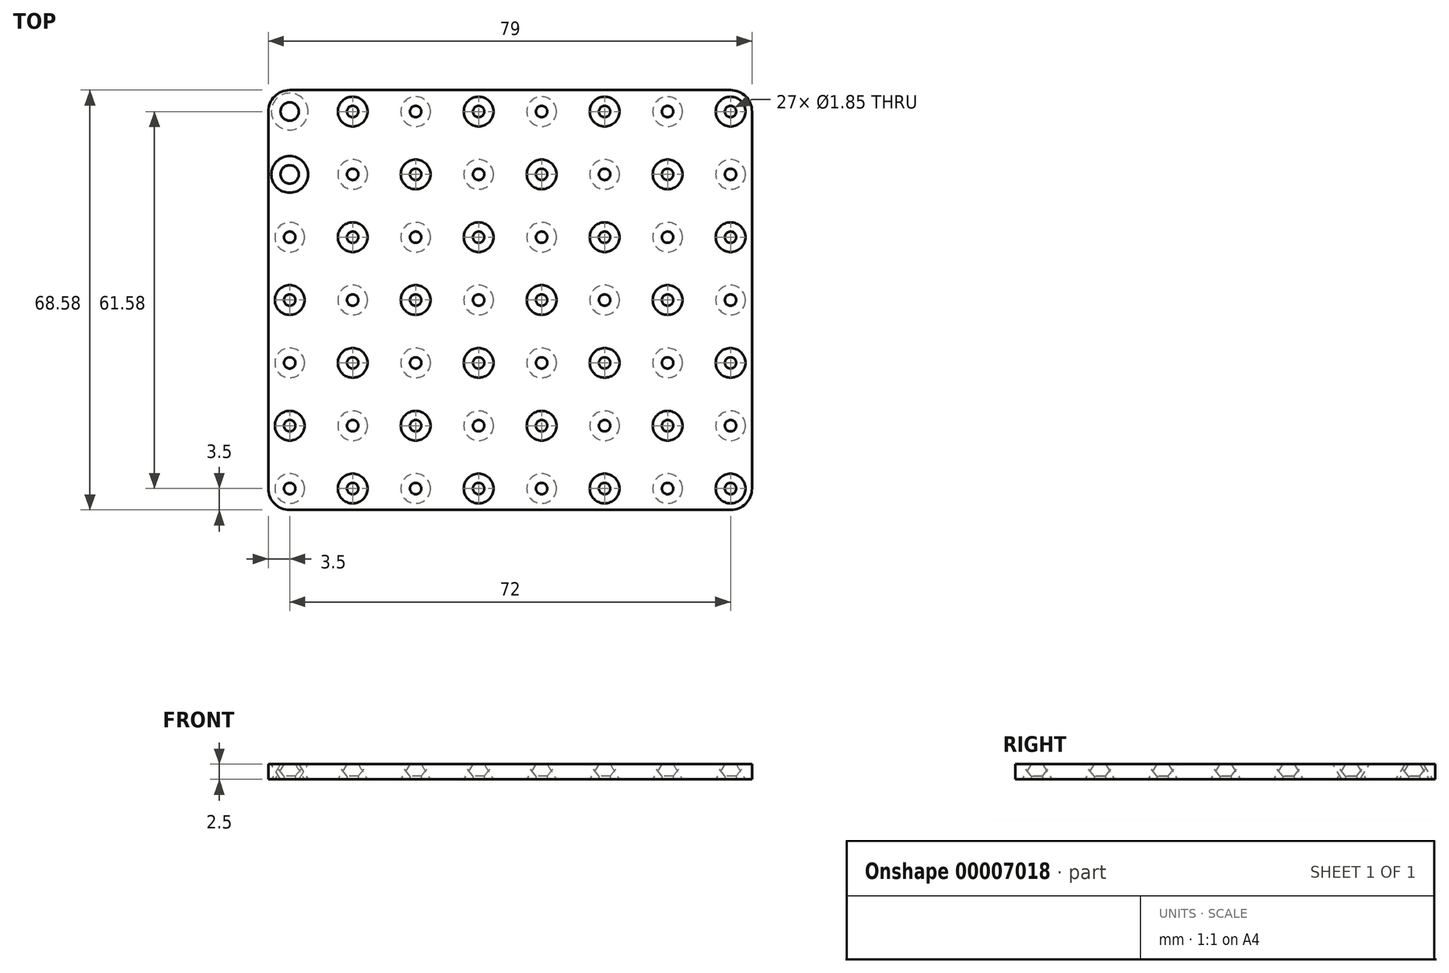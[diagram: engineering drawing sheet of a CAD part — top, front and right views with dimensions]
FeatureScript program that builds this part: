
annotation { "Feature Type Name" : "Feature", "Feature Type Description" : "" }
export const myFeature = defineFeature(function(context is Context, id is Id, definition is map)
    precondition{}
    {
        {
            var Q0;
            Q0=qCreatedBy(makeId("Top.planeOp"),FACE);
            var sketch = newSketch(context, id + "F0", { "sketchPlane" : qUnion([Q0])});
            skLineSegment(sketch, "E0.rect.bottom", {"start": v(39.5, 34.3) * mm, "end": v(-39.5, 34.3) * mm});
            skLineSegment(sketch, "E0.rect.top", {"start": v(39.5, -34.3) * mm, "end": v(-39.5, -34.3) * mm});
            skLineSegment(sketch, "E0.rect.left", {"start": v(39.5, 34.3) * mm, "end": v(39.5, -34.3) * mm});
            skLineSegment(sketch, "E0.rect.right", {"start": v(-39.5, 34.3) * mm, "end": v(-39.5, -34.3) * mm});
            skPoint(sketch, "E0.rect.middle", {"position": v(0, 0) * mm});
            skCircle(sketch, "E1", {"center": v(36, 30.8) * mm, "radius": 0.93 * mm});
            skCircle(sketch, "E2.0.1.0", {"center": v(36, 20.53) * mm, "radius": 0.93 * mm});
            skCircle(sketch, "E2.0.2.0", {"center": v(36, 10.26) * mm, "radius": 0.93 * mm});
            skCircle(sketch, "E2.0.3.0", {"center": v(36, 0) * mm, "radius": 0.93 * mm});
            skCircle(sketch, "E2.0.4.0", {"center": v(36, -10.26) * mm, "radius": 0.93 * mm});
            skCircle(sketch, "E2.0.5.0", {"center": v(36, -20.53) * mm, "radius": 0.93 * mm});
            skCircle(sketch, "E2.0.6.0", {"center": v(36, -30.8) * mm, "radius": 0.93 * mm});
            skCircle(sketch, "E2.1.0.0", {"center": v(25.71, 30.8) * mm, "radius": 0.93 * mm});
            skCircle(sketch, "E2.1.1.0", {"center": v(25.71, 20.53) * mm, "radius": 0.93 * mm});
            skCircle(sketch, "E2.1.2.0", {"center": v(25.71, 10.26) * mm, "radius": 0.93 * mm});
            skCircle(sketch, "E2.1.3.0", {"center": v(25.71, 0) * mm, "radius": 0.93 * mm});
            skCircle(sketch, "E2.1.4.0", {"center": v(25.71, -10.26) * mm, "radius": 0.93 * mm});
            skCircle(sketch, "E2.1.5.0", {"center": v(25.71, -20.53) * mm, "radius": 0.93 * mm});
            skCircle(sketch, "E2.1.6.0", {"center": v(25.71, -30.8) * mm, "radius": 0.93 * mm});
            skCircle(sketch, "E2.2.0.0", {"center": v(15.43, 30.8) * mm, "radius": 0.93 * mm});
            skCircle(sketch, "E2.2.1.0", {"center": v(15.43, 20.53) * mm, "radius": 0.93 * mm});
            skCircle(sketch, "E2.2.2.0", {"center": v(15.43, 10.26) * mm, "radius": 0.93 * mm});
            skCircle(sketch, "E2.2.3.0", {"center": v(15.43, 0) * mm, "radius": 0.93 * mm});
            skCircle(sketch, "E2.2.4.0", {"center": v(15.43, -10.26) * mm, "radius": 0.93 * mm});
            skCircle(sketch, "E2.2.5.0", {"center": v(15.43, -20.53) * mm, "radius": 0.93 * mm});
            skCircle(sketch, "E2.2.6.0", {"center": v(15.43, -30.8) * mm, "radius": 0.93 * mm});
            skCircle(sketch, "E2.3.0.0", {"center": v(5.14, 30.8) * mm, "radius": 0.93 * mm});
            skCircle(sketch, "E2.3.1.0", {"center": v(5.14, 20.53) * mm, "radius": 0.93 * mm});
            skCircle(sketch, "E2.3.2.0", {"center": v(5.14, 10.26) * mm, "radius": 0.93 * mm});
            skCircle(sketch, "E2.3.3.0", {"center": v(5.14, 0) * mm, "radius": 0.93 * mm});
            skCircle(sketch, "E2.3.4.0", {"center": v(5.14, -10.26) * mm, "radius": 0.93 * mm});
            skCircle(sketch, "E2.3.5.0", {"center": v(5.14, -20.53) * mm, "radius": 0.93 * mm});
            skCircle(sketch, "E2.3.6.0", {"center": v(5.14, -30.8) * mm, "radius": 0.93 * mm});
            skCircle(sketch, "E2.4.0.0", {"center": v(-5.14, 30.8) * mm, "radius": 0.93 * mm});
            skCircle(sketch, "E2.4.1.0", {"center": v(-5.14, 20.53) * mm, "radius": 0.93 * mm});
            skCircle(sketch, "E2.4.2.0", {"center": v(-5.14, 10.26) * mm, "radius": 0.93 * mm});
            skCircle(sketch, "E2.4.3.0", {"center": v(-5.14, 0) * mm, "radius": 0.93 * mm});
            skCircle(sketch, "E2.4.4.0", {"center": v(-5.14, -10.26) * mm, "radius": 0.93 * mm});
            skCircle(sketch, "E2.4.5.0", {"center": v(-5.14, -20.53) * mm, "radius": 0.93 * mm});
            skCircle(sketch, "E2.4.6.0", {"center": v(-5.14, -30.8) * mm, "radius": 0.93 * mm});
            skCircle(sketch, "E2.5.0.0", {"center": v(-15.43, 30.8) * mm, "radius": 0.93 * mm});
            skCircle(sketch, "E2.5.1.0", {"center": v(-15.43, 20.53) * mm, "radius": 0.93 * mm});
            skCircle(sketch, "E2.5.2.0", {"center": v(-15.43, 10.26) * mm, "radius": 0.93 * mm});
            skCircle(sketch, "E2.5.3.0", {"center": v(-15.43, 0) * mm, "radius": 0.93 * mm});
            skCircle(sketch, "E2.5.4.0", {"center": v(-15.43, -10.26) * mm, "radius": 0.93 * mm});
            skCircle(sketch, "E2.5.5.0", {"center": v(-15.43, -20.53) * mm, "radius": 0.93 * mm});
            skCircle(sketch, "E2.5.6.0", {"center": v(-15.43, -30.8) * mm, "radius": 0.93 * mm});
            skCircle(sketch, "E2.6.0.0", {"center": v(-25.71, 30.8) * mm, "radius": 0.93 * mm});
            skCircle(sketch, "E2.6.1.0", {"center": v(-25.71, 20.53) * mm, "radius": 0.93 * mm});
            skCircle(sketch, "E2.6.2.0", {"center": v(-25.71, 10.26) * mm, "radius": 0.93 * mm});
            skCircle(sketch, "E2.6.3.0", {"center": v(-25.71, 0) * mm, "radius": 0.93 * mm});
            skCircle(sketch, "E2.6.4.0", {"center": v(-25.71, -10.26) * mm, "radius": 0.93 * mm});
            skCircle(sketch, "E2.6.5.0", {"center": v(-25.71, -20.53) * mm, "radius": 0.93 * mm});
            skCircle(sketch, "E2.6.6.0", {"center": v(-25.71, -30.8) * mm, "radius": 0.93 * mm});
            skLineSegment(sketch, "E2.direction1", {"start": v(36, 30.8) * mm, "end": v(25.71, 30.8) * mm, "construction": true});
            skLineSegment(sketch, "E2.direction2", {"start": v(36, 30.8) * mm, "end": v(36, 20.53) * mm, "construction": true});
            skCircle(sketch, "E3.0.7.0", {"center": v(-36, 30.8) * mm, "radius": 0.93 * mm});
            skCircle(sketch, "E3.0.7.1", {"center": v(-36, 20.53) * mm, "radius": 0.93 * mm});
            skCircle(sketch, "E3.0.7.2", {"center": v(-36, 10.26) * mm, "radius": 0.93 * mm});
            skCircle(sketch, "E3.0.7.3", {"center": v(-36, 0) * mm, "radius": 0.93 * mm});
            skCircle(sketch, "E3.0.7.4", {"center": v(-36, -10.26) * mm, "radius": 0.93 * mm});
            skCircle(sketch, "E3.0.7.5", {"center": v(-36, -20.53) * mm, "radius": 0.93 * mm});
            skCircle(sketch, "E3.0.7.6", {"center": v(-36, -30.8) * mm, "radius": 0.93 * mm});
            skSolve(sketch);
        }
        {
            var Q0;
            Q0=makeQuery(id+"F0.imprint","IMPRINT",FACE,{"disambiguationData":[TD([[makeQuery(id+"F0.imprint","IMPRINT",EDGE,{"derivedFrom":sQuery(id+"F0.wireOp",EDGE,"E0.rect.bottom")}),1.0]])]});
            extrude(context, id + "F1", {"entities" : qUnion([Q0]), "endBound" : BoundingType.SYMMETRIC, "depth" : 2.5 * mm});
        }
        {
            var Q0;
            Q0=makeQuery(id+"F1.opExtrude","SWEPT_EDGE",EDGE,{"disambiguationData":[OSD([sQuery(id+"F0.wireOp",EDGE,"E0.rect.top"),sQuery(id+"F0.wireOp",EDGE,"E0.rect.left")])]});
            var Q1;
            Q1=makeQuery(id+"F1.opExtrude","SWEPT_EDGE",EDGE,{"disambiguationData":[OSD([sQuery(id+"F0.wireOp",EDGE,"E0.rect.top"),sQuery(id+"F0.wireOp",EDGE,"E0.rect.right")])]});
            var Q2;
            Q2=makeQuery(id+"F1.opExtrude","SWEPT_EDGE",EDGE,{"disambiguationData":[OSD([sQuery(id+"F0.wireOp",EDGE,"E0.rect.bottom"),sQuery(id+"F0.wireOp",EDGE,"E0.rect.right")])]});
            var Q3;
            Q3=makeQuery(id+"F1.opExtrude","SWEPT_EDGE",EDGE,{"disambiguationData":[OSD([sQuery(id+"F0.wireOp",EDGE,"E0.rect.bottom"),sQuery(id+"F0.wireOp",EDGE,"E0.rect.left")])]});
            fillet(context, id + "F2", {"entities" : qUnion([Q0, Q1, Q2, Q3]), "radius" : 3.5 * mm, "tangentPropagation" : true, "allowEdgeOverflow" : false});
        }
        {
            var Q0;
            {var subQ0=sQuery(id+"F0.wireOp",EDGE,"E0.rect.bottom");var subQ1=sQuery(id+"F0.wireOp",EDGE,"E0.rect.right");Q0=makeQuery(id+"F2.opFillet","BLEND_VERTEX",VERTEX,{"blendedFrom":[makeQuery(id+"F1.opExtrude","SWEPT_EDGE",EDGE,{"disambiguationData":[OSD([subQ0,subQ1])]}),makeQuery(id+"F1.opExtrude","SWEPT_FACE",FACE,{"disambiguationData":[OSD([subQ0])]}),makeQuery(id+"F1.opExtrude","CAP_FACE",FACE,{"disambiguationData":[OSD([subQ0,sQuery(id+"F0.wireOp",EDGE,"E0.rect.top"),sQuery(id+"F0.wireOp",EDGE,"E0.rect.left"),subQ1,sQuery(id+"F0.wireOp",EDGE,"E1"),sQuery(id+"F0.wireOp",EDGE,"E2.0.1.0"),sQuery(id+"F0.wireOp",EDGE,"E2.0.2.0"),sQuery(id+"F0.wireOp",EDGE,"E2.0.3.0"),sQuery(id+"F0.wireOp",EDGE,"E2.0.4.0"),sQuery(id+"F0.wireOp",EDGE,"E2.0.5.0"),sQuery(id+"F0.wireOp",EDGE,"E2.0.6.0"),sQuery(id+"F0.wireOp",EDGE,"E2.0.7.0"),sQuery(id+"F0.wireOp",EDGE,"E2.1.0.0"),sQuery(id+"F0.wireOp",EDGE,"E2.1.1.0"),sQuery(id+"F0.wireOp",EDGE,"E2.1.2.0"),sQuery(id+"F0.wireOp",EDGE,"E2.1.3.0"),sQuery(id+"F0.wireOp",EDGE,"E2.1.4.0"),sQuery(id+"F0.wireOp",EDGE,"E2.1.5.0"),sQuery(id+"F0.wireOp",EDGE,"E2.1.6.0"),sQuery(id+"F0.wireOp",EDGE,"E2.1.7.0"),sQuery(id+"F0.wireOp",EDGE,"E2.2.0.0"),sQuery(id+"F0.wireOp",EDGE,"E2.2.1.0"),sQuery(id+"F0.wireOp",EDGE,"E2.2.2.0"),sQuery(id+"F0.wireOp",EDGE,"E2.2.3.0"),sQuery(id+"F0.wireOp",EDGE,"E2.2.4.0"),sQuery(id+"F0.wireOp",EDGE,"E2.2.5.0"),sQuery(id+"F0.wireOp",EDGE,"E2.2.6.0"),sQuery(id+"F0.wireOp",EDGE,"E2.2.7.0"),sQuery(id+"F0.wireOp",EDGE,"E2.3.0.0"),sQuery(id+"F0.wireOp",EDGE,"E2.3.1.0"),sQuery(id+"F0.wireOp",EDGE,"E2.3.2.0"),sQuery(id+"F0.wireOp",EDGE,"E2.3.3.0"),sQuery(id+"F0.wireOp",EDGE,"E2.3.4.0"),sQuery(id+"F0.wireOp",EDGE,"E2.3.5.0"),sQuery(id+"F0.wireOp",EDGE,"E2.3.6.0"),sQuery(id+"F0.wireOp",EDGE,"E2.3.7.0"),sQuery(id+"F0.wireOp",EDGE,"E2.4.0.0"),sQuery(id+"F0.wireOp",EDGE,"E2.4.1.0"),sQuery(id+"F0.wireOp",EDGE,"E2.4.2.0"),sQuery(id+"F0.wireOp",EDGE,"E2.4.3.0"),sQuery(id+"F0.wireOp",EDGE,"E2.4.4.0"),sQuery(id+"F0.wireOp",EDGE,"E2.4.5.0"),sQuery(id+"F0.wireOp",EDGE,"E2.4.6.0"),sQuery(id+"F0.wireOp",EDGE,"E2.4.7.0"),sQuery(id+"F0.wireOp",EDGE,"E2.5.0.0"),sQuery(id+"F0.wireOp",EDGE,"E2.5.1.0"),sQuery(id+"F0.wireOp",EDGE,"E2.5.2.0"),sQuery(id+"F0.wireOp",EDGE,"E2.5.3.0"),sQuery(id+"F0.wireOp",EDGE,"E2.5.4.0"),sQuery(id+"F0.wireOp",EDGE,"E2.5.5.0"),sQuery(id+"F0.wireOp",EDGE,"E2.5.6.0"),sQuery(id+"F0.wireOp",EDGE,"E2.5.7.0"),sQuery(id+"F0.wireOp",EDGE,"E2.6.0.0"),sQuery(id+"F0.wireOp",EDGE,"E2.6.1.0"),sQuery(id+"F0.wireOp",EDGE,"E2.6.2.0"),sQuery(id+"F0.wireOp",EDGE,"E2.6.3.0"),sQuery(id+"F0.wireOp",EDGE,"E2.6.4.0"),sQuery(id+"F0.wireOp",EDGE,"E2.6.5.0"),sQuery(id+"F0.wireOp",EDGE,"E2.6.6.0"),sQuery(id+"F0.wireOp",EDGE,"E2.6.7.0")])],"isStart":true})],"blendedInto":[makeQuery(id+"F1.opExtrude","SWEPT_FACE",FACE,{"disambiguationData":[OSD([subQ0])]}),makeQuery(id+"F1.opExtrude","CAP_FACE",FACE,{"disambiguationData":[OSD([subQ0,sQuery(id+"F0.wireOp",EDGE,"E0.rect.top"),sQuery(id+"F0.wireOp",EDGE,"E0.rect.left"),subQ1,sQuery(id+"F0.wireOp",EDGE,"E1"),sQuery(id+"F0.wireOp",EDGE,"E2.0.1.0"),sQuery(id+"F0.wireOp",EDGE,"E2.0.2.0"),sQuery(id+"F0.wireOp",EDGE,"E2.0.3.0"),sQuery(id+"F0.wireOp",EDGE,"E2.0.4.0"),sQuery(id+"F0.wireOp",EDGE,"E2.0.5.0"),sQuery(id+"F0.wireOp",EDGE,"E2.0.6.0"),sQuery(id+"F0.wireOp",EDGE,"E2.0.7.0"),sQuery(id+"F0.wireOp",EDGE,"E2.1.0.0"),sQuery(id+"F0.wireOp",EDGE,"E2.1.1.0"),sQuery(id+"F0.wireOp",EDGE,"E2.1.2.0"),sQuery(id+"F0.wireOp",EDGE,"E2.1.3.0"),sQuery(id+"F0.wireOp",EDGE,"E2.1.4.0"),sQuery(id+"F0.wireOp",EDGE,"E2.1.5.0"),sQuery(id+"F0.wireOp",EDGE,"E2.1.6.0"),sQuery(id+"F0.wireOp",EDGE,"E2.1.7.0"),sQuery(id+"F0.wireOp",EDGE,"E2.2.0.0"),sQuery(id+"F0.wireOp",EDGE,"E2.2.1.0"),sQuery(id+"F0.wireOp",EDGE,"E2.2.2.0"),sQuery(id+"F0.wireOp",EDGE,"E2.2.3.0"),sQuery(id+"F0.wireOp",EDGE,"E2.2.4.0"),sQuery(id+"F0.wireOp",EDGE,"E2.2.5.0"),sQuery(id+"F0.wireOp",EDGE,"E2.2.6.0"),sQuery(id+"F0.wireOp",EDGE,"E2.2.7.0"),sQuery(id+"F0.wireOp",EDGE,"E2.3.0.0"),sQuery(id+"F0.wireOp",EDGE,"E2.3.1.0"),sQuery(id+"F0.wireOp",EDGE,"E2.3.2.0"),sQuery(id+"F0.wireOp",EDGE,"E2.3.3.0"),sQuery(id+"F0.wireOp",EDGE,"E2.3.4.0"),sQuery(id+"F0.wireOp",EDGE,"E2.3.5.0"),sQuery(id+"F0.wireOp",EDGE,"E2.3.6.0"),sQuery(id+"F0.wireOp",EDGE,"E2.3.7.0"),sQuery(id+"F0.wireOp",EDGE,"E2.4.0.0"),sQuery(id+"F0.wireOp",EDGE,"E2.4.1.0"),sQuery(id+"F0.wireOp",EDGE,"E2.4.2.0"),sQuery(id+"F0.wireOp",EDGE,"E2.4.3.0"),sQuery(id+"F0.wireOp",EDGE,"E2.4.4.0"),sQuery(id+"F0.wireOp",EDGE,"E2.4.5.0"),sQuery(id+"F0.wireOp",EDGE,"E2.4.6.0"),sQuery(id+"F0.wireOp",EDGE,"E2.4.7.0"),sQuery(id+"F0.wireOp",EDGE,"E2.5.0.0"),sQuery(id+"F0.wireOp",EDGE,"E2.5.1.0"),sQuery(id+"F0.wireOp",EDGE,"E2.5.2.0"),sQuery(id+"F0.wireOp",EDGE,"E2.5.3.0"),sQuery(id+"F0.wireOp",EDGE,"E2.5.4.0"),sQuery(id+"F0.wireOp",EDGE,"E2.5.5.0"),sQuery(id+"F0.wireOp",EDGE,"E2.5.6.0"),sQuery(id+"F0.wireOp",EDGE,"E2.5.7.0"),sQuery(id+"F0.wireOp",EDGE,"E2.6.0.0"),sQuery(id+"F0.wireOp",EDGE,"E2.6.1.0"),sQuery(id+"F0.wireOp",EDGE,"E2.6.2.0"),sQuery(id+"F0.wireOp",EDGE,"E2.6.3.0"),sQuery(id+"F0.wireOp",EDGE,"E2.6.4.0"),sQuery(id+"F0.wireOp",EDGE,"E2.6.5.0"),sQuery(id+"F0.wireOp",EDGE,"E2.6.6.0"),sQuery(id+"F0.wireOp",EDGE,"E2.6.7.0")])],"isStart":true})]});}
            var Q1;
            {var subQ0=sQuery(id+"F0.wireOp",EDGE,"E0.rect.bottom");var subQ1=sQuery(id+"F0.wireOp",EDGE,"E0.rect.right");Q1=makeQuery(id+"F2.opFillet","BLEND_VERTEX",VERTEX,{"blendedFrom":[makeQuery(id+"F1.opExtrude","SWEPT_EDGE",EDGE,{"disambiguationData":[OSD([subQ0,subQ1])]}),makeQuery(id+"F1.opExtrude","SWEPT_FACE",FACE,{"disambiguationData":[OSD([subQ0])]}),makeQuery(id+"F1.opExtrude","CAP_FACE",FACE,{"disambiguationData":[OSD([subQ0,sQuery(id+"F0.wireOp",EDGE,"E0.rect.top"),sQuery(id+"F0.wireOp",EDGE,"E0.rect.left"),subQ1,sQuery(id+"F0.wireOp",EDGE,"E1"),sQuery(id+"F0.wireOp",EDGE,"E2.0.1.0"),sQuery(id+"F0.wireOp",EDGE,"E2.0.2.0"),sQuery(id+"F0.wireOp",EDGE,"E2.0.3.0"),sQuery(id+"F0.wireOp",EDGE,"E2.0.4.0"),sQuery(id+"F0.wireOp",EDGE,"E2.0.5.0"),sQuery(id+"F0.wireOp",EDGE,"E2.0.6.0"),sQuery(id+"F0.wireOp",EDGE,"E2.0.7.0"),sQuery(id+"F0.wireOp",EDGE,"E2.1.0.0"),sQuery(id+"F0.wireOp",EDGE,"E2.1.1.0"),sQuery(id+"F0.wireOp",EDGE,"E2.1.2.0"),sQuery(id+"F0.wireOp",EDGE,"E2.1.3.0"),sQuery(id+"F0.wireOp",EDGE,"E2.1.4.0"),sQuery(id+"F0.wireOp",EDGE,"E2.1.5.0"),sQuery(id+"F0.wireOp",EDGE,"E2.1.6.0"),sQuery(id+"F0.wireOp",EDGE,"E2.1.7.0"),sQuery(id+"F0.wireOp",EDGE,"E2.2.0.0"),sQuery(id+"F0.wireOp",EDGE,"E2.2.1.0"),sQuery(id+"F0.wireOp",EDGE,"E2.2.2.0"),sQuery(id+"F0.wireOp",EDGE,"E2.2.3.0"),sQuery(id+"F0.wireOp",EDGE,"E2.2.4.0"),sQuery(id+"F0.wireOp",EDGE,"E2.2.5.0"),sQuery(id+"F0.wireOp",EDGE,"E2.2.6.0"),sQuery(id+"F0.wireOp",EDGE,"E2.2.7.0"),sQuery(id+"F0.wireOp",EDGE,"E2.3.0.0"),sQuery(id+"F0.wireOp",EDGE,"E2.3.1.0"),sQuery(id+"F0.wireOp",EDGE,"E2.3.2.0"),sQuery(id+"F0.wireOp",EDGE,"E2.3.3.0"),sQuery(id+"F0.wireOp",EDGE,"E2.3.4.0"),sQuery(id+"F0.wireOp",EDGE,"E2.3.5.0"),sQuery(id+"F0.wireOp",EDGE,"E2.3.6.0"),sQuery(id+"F0.wireOp",EDGE,"E2.3.7.0"),sQuery(id+"F0.wireOp",EDGE,"E2.4.0.0"),sQuery(id+"F0.wireOp",EDGE,"E2.4.1.0"),sQuery(id+"F0.wireOp",EDGE,"E2.4.2.0"),sQuery(id+"F0.wireOp",EDGE,"E2.4.3.0"),sQuery(id+"F0.wireOp",EDGE,"E2.4.4.0"),sQuery(id+"F0.wireOp",EDGE,"E2.4.5.0"),sQuery(id+"F0.wireOp",EDGE,"E2.4.6.0"),sQuery(id+"F0.wireOp",EDGE,"E2.4.7.0"),sQuery(id+"F0.wireOp",EDGE,"E2.5.0.0"),sQuery(id+"F0.wireOp",EDGE,"E2.5.1.0"),sQuery(id+"F0.wireOp",EDGE,"E2.5.2.0"),sQuery(id+"F0.wireOp",EDGE,"E2.5.3.0"),sQuery(id+"F0.wireOp",EDGE,"E2.5.4.0"),sQuery(id+"F0.wireOp",EDGE,"E2.5.5.0"),sQuery(id+"F0.wireOp",EDGE,"E2.5.6.0"),sQuery(id+"F0.wireOp",EDGE,"E2.5.7.0"),sQuery(id+"F0.wireOp",EDGE,"E2.6.0.0"),sQuery(id+"F0.wireOp",EDGE,"E2.6.1.0"),sQuery(id+"F0.wireOp",EDGE,"E2.6.2.0"),sQuery(id+"F0.wireOp",EDGE,"E2.6.3.0"),sQuery(id+"F0.wireOp",EDGE,"E2.6.4.0"),sQuery(id+"F0.wireOp",EDGE,"E2.6.5.0"),sQuery(id+"F0.wireOp",EDGE,"E2.6.6.0"),sQuery(id+"F0.wireOp",EDGE,"E2.6.7.0")])],"isStart":false})],"blendedInto":[makeQuery(id+"F1.opExtrude","SWEPT_FACE",FACE,{"disambiguationData":[OSD([subQ0])]}),makeQuery(id+"F1.opExtrude","CAP_FACE",FACE,{"disambiguationData":[OSD([subQ0,sQuery(id+"F0.wireOp",EDGE,"E0.rect.top"),sQuery(id+"F0.wireOp",EDGE,"E0.rect.left"),subQ1,sQuery(id+"F0.wireOp",EDGE,"E1"),sQuery(id+"F0.wireOp",EDGE,"E2.0.1.0"),sQuery(id+"F0.wireOp",EDGE,"E2.0.2.0"),sQuery(id+"F0.wireOp",EDGE,"E2.0.3.0"),sQuery(id+"F0.wireOp",EDGE,"E2.0.4.0"),sQuery(id+"F0.wireOp",EDGE,"E2.0.5.0"),sQuery(id+"F0.wireOp",EDGE,"E2.0.6.0"),sQuery(id+"F0.wireOp",EDGE,"E2.0.7.0"),sQuery(id+"F0.wireOp",EDGE,"E2.1.0.0"),sQuery(id+"F0.wireOp",EDGE,"E2.1.1.0"),sQuery(id+"F0.wireOp",EDGE,"E2.1.2.0"),sQuery(id+"F0.wireOp",EDGE,"E2.1.3.0"),sQuery(id+"F0.wireOp",EDGE,"E2.1.4.0"),sQuery(id+"F0.wireOp",EDGE,"E2.1.5.0"),sQuery(id+"F0.wireOp",EDGE,"E2.1.6.0"),sQuery(id+"F0.wireOp",EDGE,"E2.1.7.0"),sQuery(id+"F0.wireOp",EDGE,"E2.2.0.0"),sQuery(id+"F0.wireOp",EDGE,"E2.2.1.0"),sQuery(id+"F0.wireOp",EDGE,"E2.2.2.0"),sQuery(id+"F0.wireOp",EDGE,"E2.2.3.0"),sQuery(id+"F0.wireOp",EDGE,"E2.2.4.0"),sQuery(id+"F0.wireOp",EDGE,"E2.2.5.0"),sQuery(id+"F0.wireOp",EDGE,"E2.2.6.0"),sQuery(id+"F0.wireOp",EDGE,"E2.2.7.0"),sQuery(id+"F0.wireOp",EDGE,"E2.3.0.0"),sQuery(id+"F0.wireOp",EDGE,"E2.3.1.0"),sQuery(id+"F0.wireOp",EDGE,"E2.3.2.0"),sQuery(id+"F0.wireOp",EDGE,"E2.3.3.0"),sQuery(id+"F0.wireOp",EDGE,"E2.3.4.0"),sQuery(id+"F0.wireOp",EDGE,"E2.3.5.0"),sQuery(id+"F0.wireOp",EDGE,"E2.3.6.0"),sQuery(id+"F0.wireOp",EDGE,"E2.3.7.0"),sQuery(id+"F0.wireOp",EDGE,"E2.4.0.0"),sQuery(id+"F0.wireOp",EDGE,"E2.4.1.0"),sQuery(id+"F0.wireOp",EDGE,"E2.4.2.0"),sQuery(id+"F0.wireOp",EDGE,"E2.4.3.0"),sQuery(id+"F0.wireOp",EDGE,"E2.4.4.0"),sQuery(id+"F0.wireOp",EDGE,"E2.4.5.0"),sQuery(id+"F0.wireOp",EDGE,"E2.4.6.0"),sQuery(id+"F0.wireOp",EDGE,"E2.4.7.0"),sQuery(id+"F0.wireOp",EDGE,"E2.5.0.0"),sQuery(id+"F0.wireOp",EDGE,"E2.5.1.0"),sQuery(id+"F0.wireOp",EDGE,"E2.5.2.0"),sQuery(id+"F0.wireOp",EDGE,"E2.5.3.0"),sQuery(id+"F0.wireOp",EDGE,"E2.5.4.0"),sQuery(id+"F0.wireOp",EDGE,"E2.5.5.0"),sQuery(id+"F0.wireOp",EDGE,"E2.5.6.0"),sQuery(id+"F0.wireOp",EDGE,"E2.5.7.0"),sQuery(id+"F0.wireOp",EDGE,"E2.6.0.0"),sQuery(id+"F0.wireOp",EDGE,"E2.6.1.0"),sQuery(id+"F0.wireOp",EDGE,"E2.6.2.0"),sQuery(id+"F0.wireOp",EDGE,"E2.6.3.0"),sQuery(id+"F0.wireOp",EDGE,"E2.6.4.0"),sQuery(id+"F0.wireOp",EDGE,"E2.6.5.0"),sQuery(id+"F0.wireOp",EDGE,"E2.6.6.0"),sQuery(id+"F0.wireOp",EDGE,"E2.6.7.0")])],"isStart":false})]});}
            var Q2;
            {var subQ0=sQuery(id+"F0.wireOp",EDGE,"E0.rect.top");var subQ1=sQuery(id+"F0.wireOp",EDGE,"E0.rect.right");Q2=makeQuery(id+"F2.opFillet","BLEND_VERTEX",VERTEX,{"blendedFrom":[makeQuery(id+"F1.opExtrude","SWEPT_EDGE",EDGE,{"disambiguationData":[OSD([subQ0,subQ1])]}),makeQuery(id+"F1.opExtrude","CAP_FACE",FACE,{"disambiguationData":[OSD([sQuery(id+"F0.wireOp",EDGE,"E0.rect.bottom"),subQ0,sQuery(id+"F0.wireOp",EDGE,"E0.rect.left"),subQ1,sQuery(id+"F0.wireOp",EDGE,"E1"),sQuery(id+"F0.wireOp",EDGE,"E2.0.1.0"),sQuery(id+"F0.wireOp",EDGE,"E2.0.2.0"),sQuery(id+"F0.wireOp",EDGE,"E2.0.3.0"),sQuery(id+"F0.wireOp",EDGE,"E2.0.4.0"),sQuery(id+"F0.wireOp",EDGE,"E2.0.5.0"),sQuery(id+"F0.wireOp",EDGE,"E2.0.6.0"),sQuery(id+"F0.wireOp",EDGE,"E2.0.7.0"),sQuery(id+"F0.wireOp",EDGE,"E2.1.0.0"),sQuery(id+"F0.wireOp",EDGE,"E2.1.1.0"),sQuery(id+"F0.wireOp",EDGE,"E2.1.2.0"),sQuery(id+"F0.wireOp",EDGE,"E2.1.3.0"),sQuery(id+"F0.wireOp",EDGE,"E2.1.4.0"),sQuery(id+"F0.wireOp",EDGE,"E2.1.5.0"),sQuery(id+"F0.wireOp",EDGE,"E2.1.6.0"),sQuery(id+"F0.wireOp",EDGE,"E2.1.7.0"),sQuery(id+"F0.wireOp",EDGE,"E2.2.0.0"),sQuery(id+"F0.wireOp",EDGE,"E2.2.1.0"),sQuery(id+"F0.wireOp",EDGE,"E2.2.2.0"),sQuery(id+"F0.wireOp",EDGE,"E2.2.3.0"),sQuery(id+"F0.wireOp",EDGE,"E2.2.4.0"),sQuery(id+"F0.wireOp",EDGE,"E2.2.5.0"),sQuery(id+"F0.wireOp",EDGE,"E2.2.6.0"),sQuery(id+"F0.wireOp",EDGE,"E2.2.7.0"),sQuery(id+"F0.wireOp",EDGE,"E2.3.0.0"),sQuery(id+"F0.wireOp",EDGE,"E2.3.1.0"),sQuery(id+"F0.wireOp",EDGE,"E2.3.2.0"),sQuery(id+"F0.wireOp",EDGE,"E2.3.3.0"),sQuery(id+"F0.wireOp",EDGE,"E2.3.4.0"),sQuery(id+"F0.wireOp",EDGE,"E2.3.5.0"),sQuery(id+"F0.wireOp",EDGE,"E2.3.6.0"),sQuery(id+"F0.wireOp",EDGE,"E2.3.7.0"),sQuery(id+"F0.wireOp",EDGE,"E2.4.0.0"),sQuery(id+"F0.wireOp",EDGE,"E2.4.1.0"),sQuery(id+"F0.wireOp",EDGE,"E2.4.2.0"),sQuery(id+"F0.wireOp",EDGE,"E2.4.3.0"),sQuery(id+"F0.wireOp",EDGE,"E2.4.4.0"),sQuery(id+"F0.wireOp",EDGE,"E2.4.5.0"),sQuery(id+"F0.wireOp",EDGE,"E2.4.6.0"),sQuery(id+"F0.wireOp",EDGE,"E2.4.7.0"),sQuery(id+"F0.wireOp",EDGE,"E2.5.0.0"),sQuery(id+"F0.wireOp",EDGE,"E2.5.1.0"),sQuery(id+"F0.wireOp",EDGE,"E2.5.2.0"),sQuery(id+"F0.wireOp",EDGE,"E2.5.3.0"),sQuery(id+"F0.wireOp",EDGE,"E2.5.4.0"),sQuery(id+"F0.wireOp",EDGE,"E2.5.5.0"),sQuery(id+"F0.wireOp",EDGE,"E2.5.6.0"),sQuery(id+"F0.wireOp",EDGE,"E2.5.7.0"),sQuery(id+"F0.wireOp",EDGE,"E2.6.0.0"),sQuery(id+"F0.wireOp",EDGE,"E2.6.1.0"),sQuery(id+"F0.wireOp",EDGE,"E2.6.2.0"),sQuery(id+"F0.wireOp",EDGE,"E2.6.3.0"),sQuery(id+"F0.wireOp",EDGE,"E2.6.4.0"),sQuery(id+"F0.wireOp",EDGE,"E2.6.5.0"),sQuery(id+"F0.wireOp",EDGE,"E2.6.6.0"),sQuery(id+"F0.wireOp",EDGE,"E2.6.7.0")])],"isStart":false}),makeQuery(id+"F1.opExtrude","SWEPT_FACE",FACE,{"disambiguationData":[OSD([subQ0])]})],"blendedInto":[makeQuery(id+"F1.opExtrude","CAP_FACE",FACE,{"disambiguationData":[OSD([sQuery(id+"F0.wireOp",EDGE,"E0.rect.bottom"),subQ0,sQuery(id+"F0.wireOp",EDGE,"E0.rect.left"),subQ1,sQuery(id+"F0.wireOp",EDGE,"E1"),sQuery(id+"F0.wireOp",EDGE,"E2.0.1.0"),sQuery(id+"F0.wireOp",EDGE,"E2.0.2.0"),sQuery(id+"F0.wireOp",EDGE,"E2.0.3.0"),sQuery(id+"F0.wireOp",EDGE,"E2.0.4.0"),sQuery(id+"F0.wireOp",EDGE,"E2.0.5.0"),sQuery(id+"F0.wireOp",EDGE,"E2.0.6.0"),sQuery(id+"F0.wireOp",EDGE,"E2.0.7.0"),sQuery(id+"F0.wireOp",EDGE,"E2.1.0.0"),sQuery(id+"F0.wireOp",EDGE,"E2.1.1.0"),sQuery(id+"F0.wireOp",EDGE,"E2.1.2.0"),sQuery(id+"F0.wireOp",EDGE,"E2.1.3.0"),sQuery(id+"F0.wireOp",EDGE,"E2.1.4.0"),sQuery(id+"F0.wireOp",EDGE,"E2.1.5.0"),sQuery(id+"F0.wireOp",EDGE,"E2.1.6.0"),sQuery(id+"F0.wireOp",EDGE,"E2.1.7.0"),sQuery(id+"F0.wireOp",EDGE,"E2.2.0.0"),sQuery(id+"F0.wireOp",EDGE,"E2.2.1.0"),sQuery(id+"F0.wireOp",EDGE,"E2.2.2.0"),sQuery(id+"F0.wireOp",EDGE,"E2.2.3.0"),sQuery(id+"F0.wireOp",EDGE,"E2.2.4.0"),sQuery(id+"F0.wireOp",EDGE,"E2.2.5.0"),sQuery(id+"F0.wireOp",EDGE,"E2.2.6.0"),sQuery(id+"F0.wireOp",EDGE,"E2.2.7.0"),sQuery(id+"F0.wireOp",EDGE,"E2.3.0.0"),sQuery(id+"F0.wireOp",EDGE,"E2.3.1.0"),sQuery(id+"F0.wireOp",EDGE,"E2.3.2.0"),sQuery(id+"F0.wireOp",EDGE,"E2.3.3.0"),sQuery(id+"F0.wireOp",EDGE,"E2.3.4.0"),sQuery(id+"F0.wireOp",EDGE,"E2.3.5.0"),sQuery(id+"F0.wireOp",EDGE,"E2.3.6.0"),sQuery(id+"F0.wireOp",EDGE,"E2.3.7.0"),sQuery(id+"F0.wireOp",EDGE,"E2.4.0.0"),sQuery(id+"F0.wireOp",EDGE,"E2.4.1.0"),sQuery(id+"F0.wireOp",EDGE,"E2.4.2.0"),sQuery(id+"F0.wireOp",EDGE,"E2.4.3.0"),sQuery(id+"F0.wireOp",EDGE,"E2.4.4.0"),sQuery(id+"F0.wireOp",EDGE,"E2.4.5.0"),sQuery(id+"F0.wireOp",EDGE,"E2.4.6.0"),sQuery(id+"F0.wireOp",EDGE,"E2.4.7.0"),sQuery(id+"F0.wireOp",EDGE,"E2.5.0.0"),sQuery(id+"F0.wireOp",EDGE,"E2.5.1.0"),sQuery(id+"F0.wireOp",EDGE,"E2.5.2.0"),sQuery(id+"F0.wireOp",EDGE,"E2.5.3.0"),sQuery(id+"F0.wireOp",EDGE,"E2.5.4.0"),sQuery(id+"F0.wireOp",EDGE,"E2.5.5.0"),sQuery(id+"F0.wireOp",EDGE,"E2.5.6.0"),sQuery(id+"F0.wireOp",EDGE,"E2.5.7.0"),sQuery(id+"F0.wireOp",EDGE,"E2.6.0.0"),sQuery(id+"F0.wireOp",EDGE,"E2.6.1.0"),sQuery(id+"F0.wireOp",EDGE,"E2.6.2.0"),sQuery(id+"F0.wireOp",EDGE,"E2.6.3.0"),sQuery(id+"F0.wireOp",EDGE,"E2.6.4.0"),sQuery(id+"F0.wireOp",EDGE,"E2.6.5.0"),sQuery(id+"F0.wireOp",EDGE,"E2.6.6.0"),sQuery(id+"F0.wireOp",EDGE,"E2.6.7.0")])],"isStart":false}),makeQuery(id+"F1.opExtrude","SWEPT_FACE",FACE,{"disambiguationData":[OSD([subQ0])]})]});}
            cPlane(context, id + "F3", {"entities" : qUnion([Q0, Q1, Q2]), "cplaneType" : CPlaneType.THREE_POINT, "offset" : 150 * mm, "width" : 150 * mm, "height" : 150 * mm});
        }
        {
            var Q0;
            Q0=qCreatedBy(id+"F3.planeOp",FACE);
            var sketch = newSketch(context, id + "F4", { "sketchPlane" : qUnion([Q0])});
            skLineSegment(sketch, "E4", {"start": v(-33.8, -1.25) * mm, "end": v(-30.8, -1.25) * mm});
            skLineSegment(sketch, "E5", {"start": v(-30.8, 1.25) * mm, "end": v(-30.8, -1.25) * mm});
            skLineSegment(sketch, "E6", {"start": v(-33.8, -1.25) * mm, "end": v(-32.3, 1.25) * mm});
            skLineSegment(sketch, "E7", {"start": v(-32.3, 1.25) * mm, "end": v(-30.8, 1.25) * mm});
            skPoint(sketch, "E8.orphan", {"position": v(-30.8, 3.75) * mm});
            skLineSegment(sketch, "E9", {"start": v(-30.8, -1.25) * mm, "end": v(-20.53, -1.25) * mm, "construction": true});
            skLineSegment(sketch, "E10", {"start": v(-25.66, -1.25) * mm, "end": v(-25.66, 1.25) * mm, "construction": true});
            skLineSegment(sketch, "E11", {"start": v(-20.53, 1.25) * mm, "end": v(-25.66, 1.25) * mm, "construction": true});
            skLineSegment(sketch, "E12", {"start": v(-20.53, 1.25) * mm, "end": v(-20.53, -1.25) * mm});
            skLineSegment(sketch, "E13", {"start": v(-25.66, 0) * mm, "end": v(-20.53, 0) * mm, "construction": true});
            skLineSegment(sketch, "E14.0.MirrorCS", {"start": v(-17.53, -1.25) * mm, "end": v(-20.53, -1.25) * mm, "construction": true});
            skLineSegment(sketch, "E14.1.MirrorCS", {"start": v(-19.03, 1.25) * mm, "end": v(-20.53, 1.25) * mm, "construction": true});
            skLineSegment(sketch, "E14.3.MirrorCS", {"start": v(-17.53, -1.25) * mm, "end": v(-19.03, 1.25) * mm, "construction": true});
            skLineSegment(sketch, "E15.0.MirrorCS", {"start": v(-20.53, -1.25) * mm, "end": v(-20.53, 1.25) * mm});
            skLineSegment(sketch, "E15.1.MirrorCS", {"start": v(-19.03, -1.25) * mm, "end": v(-20.53, -1.25) * mm});
            skLineSegment(sketch, "E15.2.MirrorCS", {"start": v(-17.53, 1.25) * mm, "end": v(-19.03, -1.25) * mm});
            skLineSegment(sketch, "E15.3.MirrorCS", {"start": v(-20.53, -1.25) * mm, "end": v(-20.53, 1.25) * mm});
            skLineSegment(sketch, "E15.4.MirrorCS", {"start": v(-17.53, 1.25) * mm, "end": v(-20.53, 1.25) * mm});
            skSolve(sketch);
        }
        {
            var Q0;
            Q0=makeQuery(id+"F4.imprint","IMPRINT",FACE,{"disambiguationData":[TD([[makeQuery(id+"F4.imprint","IMPRINT",EDGE,{"derivedFrom":sQuery(id+"F4.wireOp",EDGE,"E4")}),1.0]])]});
            var Q1;
            Q1=sQuery(id+"F4.wireOp",EDGE,"E5");
            revolve(context, id + "F5", {"operationType" : NewBodyOperationType.REMOVE, "entities" : qUnion([Q0]), "axis" : qUnion([Q1]), "revolveType" : RevolveType.FULL, "oppositeDirection" : true});
        }
        {
            var Q0;
            Q0=makeQuery(id+"F4.imprint","IMPRINT",FACE,{"disambiguationData":[TD([[makeQuery(id+"F4.imprint","IMPRINT",EDGE,{"derivedFrom":sQuery(id+"F4.wireOp",EDGE,"E15.1.MirrorCS")}),-1.0]])]});
            var Q1;
            Q1=sQuery(id+"F4.wireOp",EDGE,"E15.3.MirrorCS");
            revolve(context, id + "F6", {"operationType" : NewBodyOperationType.REMOVE, "entities" : qUnion([Q0]), "axis" : qUnion([Q1]), "revolveType" : RevolveType.FULL, "oppositeDirection" : true});
        }
        {
            var Q0;
            Q0=makeQuery(id+"F1.opExtrude","CAP_EDGE",EDGE,{"disambiguationData":[OSD([sQuery(id+"F0.wireOp",EDGE,"E2.5.0.0")])],"isStart":true});
            var Q1;
            Q1=makeQuery(id+"F1.opExtrude","CAP_EDGE",EDGE,{"disambiguationData":[OSD([sQuery(id+"F0.wireOp",EDGE,"E2.6.1.0")])],"isStart":true});
            var Q2;
            Q2=makeQuery(id+"F1.opExtrude","CAP_EDGE",EDGE,{"disambiguationData":[OSD([sQuery(id+"F0.wireOp",EDGE,"E3.0.7.2")])],"isStart":true});
            var Q3;
            Q3=makeQuery(id+"F1.opExtrude","CAP_EDGE",EDGE,{"disambiguationData":[OSD([sQuery(id+"F0.wireOp",EDGE,"E2.3.0.0")])],"isStart":true});
            var Q4;
            Q4=makeQuery(id+"F1.opExtrude","CAP_EDGE",EDGE,{"disambiguationData":[OSD([sQuery(id+"F0.wireOp",EDGE,"E2.4.1.0")])],"isStart":true});
            var Q5;
            Q5=makeQuery(id+"F1.opExtrude","CAP_EDGE",EDGE,{"disambiguationData":[OSD([sQuery(id+"F0.wireOp",EDGE,"E2.5.2.0")])],"isStart":true});
            var Q6;
            Q6=makeQuery(id+"F1.opExtrude","CAP_EDGE",EDGE,{"disambiguationData":[OSD([sQuery(id+"F0.wireOp",EDGE,"E2.6.3.0")])],"isStart":true});
            var Q7;
            Q7=makeQuery(id+"F1.opExtrude","CAP_EDGE",EDGE,{"disambiguationData":[OSD([sQuery(id+"F0.wireOp",EDGE,"E3.0.7.4")])],"isStart":true});
            var Q8;
            Q8=makeQuery(id+"F1.opExtrude","CAP_EDGE",EDGE,{"disambiguationData":[OSD([sQuery(id+"F0.wireOp",EDGE,"E3.0.7.6")])],"isStart":true});
            var Q9;
            Q9=makeQuery(id+"F1.opExtrude","CAP_EDGE",EDGE,{"disambiguationData":[OSD([sQuery(id+"F0.wireOp",EDGE,"E2.6.5.0")])],"isStart":true});
            var Q10;
            Q10=makeQuery(id+"F1.opExtrude","CAP_EDGE",EDGE,{"disambiguationData":[OSD([sQuery(id+"F0.wireOp",EDGE,"E2.5.4.0")])],"isStart":true});
            var Q11;
            Q11=makeQuery(id+"F1.opExtrude","CAP_EDGE",EDGE,{"disambiguationData":[OSD([sQuery(id+"F0.wireOp",EDGE,"E2.4.3.0")])],"isStart":true});
            var Q12;
            Q12=makeQuery(id+"F1.opExtrude","CAP_EDGE",EDGE,{"disambiguationData":[OSD([sQuery(id+"F0.wireOp",EDGE,"E2.3.2.0")])],"isStart":true});
            var Q13;
            Q13=makeQuery(id+"F1.opExtrude","CAP_EDGE",EDGE,{"disambiguationData":[OSD([sQuery(id+"F0.wireOp",EDGE,"E2.2.1.0")])],"isStart":true});
            var Q14;
            Q14=makeQuery(id+"F1.opExtrude","CAP_EDGE",EDGE,{"disambiguationData":[OSD([sQuery(id+"F0.wireOp",EDGE,"E2.1.0.0")])],"isStart":true});
            var Q15;
            Q15=makeQuery(id+"F1.opExtrude","CAP_EDGE",EDGE,{"disambiguationData":[OSD([sQuery(id+"F0.wireOp",EDGE,"E2.0.1.0")])],"isStart":true});
            var Q16;
            Q16=makeQuery(id+"F1.opExtrude","CAP_EDGE",EDGE,{"disambiguationData":[OSD([sQuery(id+"F0.wireOp",EDGE,"E2.2.3.0")])],"isStart":true});
            var Q17;
            Q17=makeQuery(id+"F1.opExtrude","CAP_EDGE",EDGE,{"disambiguationData":[OSD([sQuery(id+"F0.wireOp",EDGE,"E2.3.4.0")])],"isStart":true});
            var Q18;
            Q18=makeQuery(id+"F1.opExtrude","CAP_EDGE",EDGE,{"disambiguationData":[OSD([sQuery(id+"F0.wireOp",EDGE,"E2.4.5.0")])],"isStart":true});
            var Q19;
            Q19=makeQuery(id+"F1.opExtrude","CAP_EDGE",EDGE,{"disambiguationData":[OSD([sQuery(id+"F0.wireOp",EDGE,"E2.5.6.0")])],"isStart":true});
            var Q20;
            Q20=makeQuery(id+"F1.opExtrude","CAP_EDGE",EDGE,{"disambiguationData":[OSD([sQuery(id+"F0.wireOp",EDGE,"E2.0.3.0")])],"isStart":true});
            var Q21;
            Q21=makeQuery(id+"F1.opExtrude","CAP_EDGE",EDGE,{"disambiguationData":[OSD([sQuery(id+"F0.wireOp",EDGE,"E2.1.4.0")])],"isStart":true});
            var Q22;
            Q22=makeQuery(id+"F1.opExtrude","CAP_EDGE",EDGE,{"disambiguationData":[OSD([sQuery(id+"F0.wireOp",EDGE,"E2.2.5.0")])],"isStart":true});
            var Q23;
            Q23=makeQuery(id+"F1.opExtrude","CAP_EDGE",EDGE,{"disambiguationData":[OSD([sQuery(id+"F0.wireOp",EDGE,"E2.3.6.0")])],"isStart":true});
            var Q24;
            Q24=makeQuery(id+"F1.opExtrude","CAP_EDGE",EDGE,{"disambiguationData":[OSD([sQuery(id+"F0.wireOp",EDGE,"E2.0.5.0")])],"isStart":true});
            var Q25;
            Q25=makeQuery(id+"F1.opExtrude","CAP_EDGE",EDGE,{"disambiguationData":[OSD([sQuery(id+"F0.wireOp",EDGE,"E2.1.6.0")])],"isStart":true});
            var Q26;
            Q26=makeQuery(id+"F1.opExtrude","CAP_EDGE",EDGE,{"disambiguationData":[OSD([sQuery(id+"F0.wireOp",EDGE,"E2.1.2.0")])],"isStart":true});
            chamfer(context, id + "F7", {"entities" : qUnion([Q0, Q1, Q2, Q3, Q4, Q5, Q6, Q7, Q8, Q9, Q10, Q11, Q12, Q13, Q14, Q15, Q16, Q17, Q18, Q19, Q20, Q21, Q22, Q23, Q24, Q25, Q26]), "chamferType" : ChamferType.TWO_OFFSETS, "width1" : 1.5 * mm, "oppositeDirection" : false, "width2" : 2.5 * mm, "tangentPropagation" : true});
        }
        {
            var Q0;
            Q0=makeQuery(id+"F1.opExtrude","CAP_EDGE",EDGE,{"disambiguationData":[OSD([sQuery(id+"F0.wireOp",EDGE,"E2.6.0.0")])],"isStart":false});
            var Q1;
            Q1=makeQuery(id+"F1.opExtrude","CAP_EDGE",EDGE,{"disambiguationData":[OSD([sQuery(id+"F0.wireOp",EDGE,"E3.0.7.3")])],"isStart":false});
            var Q2;
            Q2=makeQuery(id+"F1.opExtrude","CAP_EDGE",EDGE,{"disambiguationData":[OSD([sQuery(id+"F0.wireOp",EDGE,"E2.6.2.0")])],"isStart":false});
            var Q3;
            Q3=makeQuery(id+"F1.opExtrude","CAP_EDGE",EDGE,{"disambiguationData":[OSD([sQuery(id+"F0.wireOp",EDGE,"E2.5.1.0")])],"isStart":false});
            var Q4;
            Q4=makeQuery(id+"F1.opExtrude","CAP_EDGE",EDGE,{"disambiguationData":[OSD([sQuery(id+"F0.wireOp",EDGE,"E2.4.0.0")])],"isStart":false});
            var Q5;
            Q5=makeQuery(id+"F1.opExtrude","CAP_EDGE",EDGE,{"disambiguationData":[OSD([sQuery(id+"F0.wireOp",EDGE,"E3.0.7.5")])],"isStart":false});
            var Q6;
            Q6=makeQuery(id+"F1.opExtrude","CAP_EDGE",EDGE,{"disambiguationData":[OSD([sQuery(id+"F0.wireOp",EDGE,"E2.6.4.0")])],"isStart":false});
            var Q7;
            Q7=makeQuery(id+"F1.opExtrude","CAP_EDGE",EDGE,{"disambiguationData":[OSD([sQuery(id+"F0.wireOp",EDGE,"E2.5.3.0")])],"isStart":false});
            var Q8;
            Q8=makeQuery(id+"F1.opExtrude","CAP_EDGE",EDGE,{"disambiguationData":[OSD([sQuery(id+"F0.wireOp",EDGE,"E2.4.2.0")])],"isStart":false});
            var Q9;
            Q9=makeQuery(id+"F1.opExtrude","CAP_EDGE",EDGE,{"disambiguationData":[OSD([sQuery(id+"F0.wireOp",EDGE,"E2.3.1.0")])],"isStart":false});
            var Q10;
            Q10=makeQuery(id+"F1.opExtrude","CAP_EDGE",EDGE,{"disambiguationData":[OSD([sQuery(id+"F0.wireOp",EDGE,"E2.2.0.0")])],"isStart":false});
            var Q11;
            Q11=makeQuery(id+"F1.opExtrude","CAP_EDGE",EDGE,{"disambiguationData":[OSD([sQuery(id+"F0.wireOp",EDGE,"E2.1.1.0")])],"isStart":false});
            var Q12;
            Q12=makeQuery(id+"F1.opExtrude","CAP_EDGE",EDGE,{"disambiguationData":[OSD([sQuery(id+"F0.wireOp",EDGE,"E1")])],"isStart":false});
            var Q13;
            Q13=makeQuery(id+"F1.opExtrude","CAP_EDGE",EDGE,{"disambiguationData":[OSD([sQuery(id+"F0.wireOp",EDGE,"E2.2.2.0")])],"isStart":false});
            var Q14;
            Q14=makeQuery(id+"F1.opExtrude","CAP_EDGE",EDGE,{"disambiguationData":[OSD([sQuery(id+"F0.wireOp",EDGE,"E2.3.3.0")])],"isStart":false});
            var Q15;
            Q15=makeQuery(id+"F1.opExtrude","CAP_EDGE",EDGE,{"disambiguationData":[OSD([sQuery(id+"F0.wireOp",EDGE,"E2.4.4.0")])],"isStart":false});
            var Q16;
            Q16=makeQuery(id+"F1.opExtrude","CAP_EDGE",EDGE,{"disambiguationData":[OSD([sQuery(id+"F0.wireOp",EDGE,"E2.5.5.0")])],"isStart":false});
            var Q17;
            Q17=makeQuery(id+"F1.opExtrude","CAP_EDGE",EDGE,{"disambiguationData":[OSD([sQuery(id+"F0.wireOp",EDGE,"E2.6.6.0")])],"isStart":false});
            var Q18;
            Q18=makeQuery(id+"F1.opExtrude","CAP_EDGE",EDGE,{"disambiguationData":[OSD([sQuery(id+"F0.wireOp",EDGE,"E2.1.3.0")])],"isStart":false});
            var Q19;
            Q19=makeQuery(id+"F1.opExtrude","CAP_EDGE",EDGE,{"disambiguationData":[OSD([sQuery(id+"F0.wireOp",EDGE,"E2.0.4.0")])],"isStart":false});
            var Q20;
            Q20=makeQuery(id+"F1.opExtrude","CAP_EDGE",EDGE,{"disambiguationData":[OSD([sQuery(id+"F0.wireOp",EDGE,"E2.0.2.0")])],"isStart":false});
            var Q21;
            Q21=makeQuery(id+"F1.opExtrude","CAP_EDGE",EDGE,{"disambiguationData":[OSD([sQuery(id+"F0.wireOp",EDGE,"E2.2.4.0")])],"isStart":false});
            var Q22;
            Q22=makeQuery(id+"F1.opExtrude","CAP_EDGE",EDGE,{"disambiguationData":[OSD([sQuery(id+"F0.wireOp",EDGE,"E2.1.5.0")])],"isStart":false});
            var Q23;
            Q23=makeQuery(id+"F1.opExtrude","CAP_EDGE",EDGE,{"disambiguationData":[OSD([sQuery(id+"F0.wireOp",EDGE,"E2.0.6.0")])],"isStart":false});
            var Q24;
            Q24=makeQuery(id+"F1.opExtrude","CAP_EDGE",EDGE,{"disambiguationData":[OSD([sQuery(id+"F0.wireOp",EDGE,"E2.3.5.0")])],"isStart":false});
            var Q25;
            Q25=makeQuery(id+"F1.opExtrude","CAP_EDGE",EDGE,{"disambiguationData":[OSD([sQuery(id+"F0.wireOp",EDGE,"E2.2.6.0")])],"isStart":false});
            var Q26;
            Q26=makeQuery(id+"F1.opExtrude","CAP_EDGE",EDGE,{"disambiguationData":[OSD([sQuery(id+"F0.wireOp",EDGE,"E2.4.6.0")])],"isStart":false});
            chamfer(context, id + "F8", {"entities" : qUnion([Q0, Q1, Q2, Q3, Q4, Q5, Q6, Q7, Q8, Q9, Q10, Q11, Q12, Q13, Q14, Q15, Q16, Q17, Q18, Q19, Q20, Q21, Q22, Q23, Q24, Q25, Q26]), "chamferType" : ChamferType.TWO_OFFSETS, "width1" : 2 * mm, "oppositeDirection" : false, "width2" : 1.5 * mm, "tangentPropagation" : true});
        }
    });
